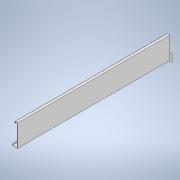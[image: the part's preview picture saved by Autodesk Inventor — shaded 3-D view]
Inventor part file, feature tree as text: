
AUTODESK INVENTOR PART (.ipt)
format: ipt  version: 2020 (Build 240168000, 168)  size: 108,032 bytes
history: native  units: mm
features: other x5, plane x1, extrude x1, sketch x1
ambient origin geometry x8: Origin, YZ Plane, XZ Plane, XY Plane, X Axis, Y Axis, Z Axis, Center Point
bodies: Body1 (feature_tree)
feature tree (8):
  plane  "Work Plane1"
  extrude  "Extrusion2"  Depth=80.0mm
  sketch  "Sketch1"  dims[d2=25.0mm d4=80.0mm d5=25.0mm d6=3.5mm d7=350.0mm d8=2417.4mm d9=0.0mm]
  parser-record x1  (decoder bookkeeping rows leaked as tree rows — omitted from the tree; the rows remain in map.json)
  other  "estufa morango 20.iam"
  other  "corners 20feet:1"
  other  "corners bottom:1"
  other  "corner_BL_MIR:1"
note: 1 file-system path scrubbed to <path> (originals preserved in map.json)
